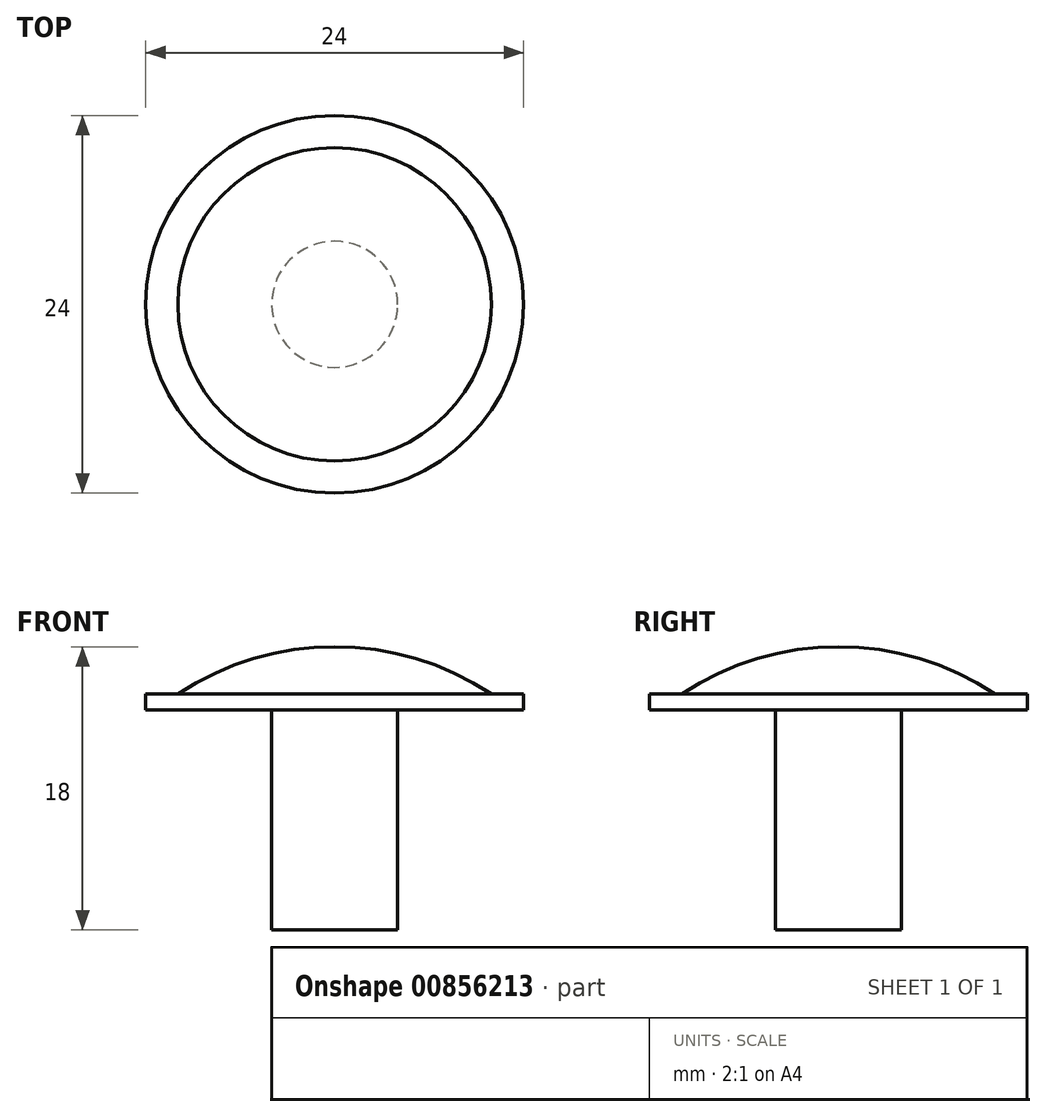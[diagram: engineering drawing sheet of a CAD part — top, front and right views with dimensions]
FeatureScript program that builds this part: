
annotation { "Feature Type Name" : "Feature", "Feature Type Description" : "" }
export const myFeature = defineFeature(function(context is Context, id is Id, definition is map)
    precondition{}
    {
        {
            var Q0;
            Q0=qCreatedBy(makeId("Top.planeOp"),FACE);
            var sketch = newSketch(context, id + "F0", { "sketchPlane" : qUnion([Q0])});
            skCircle(sketch, "E0", {"center": v(0, 0) * mm, "radius": 18 * mm});
            skLineSegment(sketch, "E1", {"start": v(0, 18) * mm, "end": v(0, -18) * mm});
            skSolve(sketch);
        }
        {
            var Q0;
            {var subQ0=sQuery(id+"F0.wireOp",EDGE,"E1");Q0=makeQuery(id+"F0.imprint","IMPRINT",FACE,{"disambiguationData":[TD([[makeQuery(id+"F0.imprint","IMPRINT",EDGE,{"derivedFrom":subQ0}),1.0]])]});}
            var Q1;
            Q1=sQuery(id+"F0.wireOp",EDGE,"E1");
            revolve(context, id + "F1", {"surfaceOperationType" : NewSurfaceOperationType.NEW, "entities" : qUnion([Q0]), "axis" : qUnion([Q1]), "revolveType" : RevolveType.ONE_DIRECTION, "angle" : 180 * degree});
        }
        {
            var Q0;
            Q0=makeQuery(id+"F1.opRevolve","CAP_FACE",FACE,{"disambiguationData":[OSD([sQuery(id+"F0.wireOp",EDGE,"E0"),sQuery(id+"F0.wireOp",EDGE,"E1")])],"isStart":true});
            var sketch = newSketch(context, id + "F2", { "sketchPlane" : qUnion([Q0])});
            skCircle(sketch, "E2", {"center": v(0, 0) * mm, "radius": 18 * mm});
            skCircle(sketch, "E3", {"center": v(0, 0) * mm, "radius": 4 * mm});
            skCircle(sketch, "E4", {"center": v(0, 0) * mm, "radius": 1.5 * mm});
            skSolve(sketch);
        }
        {
            var Q0;
            Q0 = qSketchRegion(id + "F2", true);
            extrude(context, id + "F3", {"entities" : qUnion([Q0]), "operationType" : NewBodyOperationType.REMOVE, "oppositeDirection" : true, "depth" : 14 * mm, "offsetDistance" : 25 * mm});
        }
        {
            var Q0;
            Q0=qCreatedBy(makeId("Top.planeOp"),FACE);
            cPlane(context, id + "F4", {"entities" : qUnion([Q0]), "cplaneType" : CPlaneType.OFFSET, "offset" : 14 * mm, "width" : 150 * mm, "height" : 150 * mm});
        }
        {
            var Q0;
            Q0=qCreatedBy(id+"F4.planeOp",FACE);
            var sketch = newSketch(context, id + "F5", { "sketchPlane" : qUnion([Q0])});
            skCircle(sketch, "E5", {"center": v(0, 0) * mm, "radius": 12 * mm});
            skSolve(sketch);
        }
        {
            var Q0;
            Q0 = qSketchRegion(id + "F5", true);
            extrude(context, id + "F6", {"entities" : qUnion([Q0]), "operationType" : NewBodyOperationType.ADD, "depth" : 1 * mm, "offsetDistance" : 25 * mm});
        }
        {
            var Q0;
            Q0=makeQuery(id+"F1.opRevolve","CAP_FACE",FACE,{"disambiguationData":[OSD([sQuery(id+"F0.wireOp",EDGE,"E0"),sQuery(id+"F0.wireOp",EDGE,"E1")])],"isStart":true});
            var sketch = newSketch(context, id + "F7", { "sketchPlane" : qUnion([Q0])});
            skCircle(sketch, "E6", {"center": v(0, 0) * mm, "radius": 4 * mm});
            skSolve(sketch);
        }
        {
            var Q0;
            Q0 = qSketchRegion(id + "F7", true);
            extrude(context, id + "F8", {"entities" : qUnion([Q0]), "operationType" : NewBodyOperationType.ADD, "oppositeDirection" : true, "depth" : 11 * mm, "offsetDistance" : 25 * mm});
        }
    });
